# Revit family: VZ-PORTA-FERRO SIMPLES
name_source: partatom
category: Doors
units: mm (PartAtom-declared; Revit-internal decimal feet)

## family parameters
Always vertical = Yes
Cut with Voids When Loaded = No
Host = Wall
OmniClass Number = 23.30.10.00
OmniClass Title = Doors
Room Calculation Point = No
Shared = No

## types (2) — shared parameters
Altura_Fechadura = 110 cm
Altura_Folha = 213.5 cm
Analytic Construction = <Nenhum>
Batente = 4 cm
Esp_Folha = 3.7 cm
Esp_Marco = 3.5 cm
Esp_Perfil = 0.5 cm
Function = Interior
Height = 210 cm
Largura_Folha = 87 cm
Mat_Batente = .VZ-PINTURA-ESMALTE-BRANCO CORAL CORALIT
Mat_Fechadura = .VZ-METAL-AÇO INOXIDÁVEL
Mat_Folha = .VZ-PINTURA-ESMALTE-BRANCO CORAL CORALIT
PT_ALTURA OSSO = 214 cm
PT_FECHADURAS TETRA = Yes
PT_LARGURA OSSO = 88 cm
PT_MOLA_AEREA = Yes
PT_TIPO = FERRO
Profundidade_Perfil = 4 cm
Rough Height = 214 cm
Rough Width = 88 cm
VZA_ACESSIBILIDADE = No
Wall Closure = By host
Width = 80 cm

## per-type parameters (varying)
| type | Description | Deslocamento_Fechadura | PT_HDL_C90 | PT_MAÇANETA_DESIGN_420 | PT_PUXADOR_FIXO | VZA_CODIGO CLIENTE |
| PF01-80x210 | PORTA CEGA, 01 FOLHA DE ABRIR EM AÇO DUPLA LISA, REVESTIDA EM ESMALTE BRANCO CORAL CORALIT E FIXADA COM GRAPAS METÁLICAS, COM FECHO ELÉTRICO 12V EMBUTIDO NO MARCO HDL C90 E PUXADOR FIXO PAPAIZ  (REF. 500, ACABAMENTO ACETINADO) TANTO NO LADO EXTERNO QUANTO NO LADO INTERNO DA PORTA, COM MOLA AÉREA DORMA POTÊNCIA 2, DUAS FECHADURAS TETRA COM A MESMA COMBINAÇÃO | 4.35 cm | Yes | No | Yes | PF01 |
| PF02-80x210 | PORTA CEGA, 1 FOLHA DE ABRIR DE AÇO, REVESTIDA EM ESMALTE BRANCO CORAL CORALIT, DOBRADIÇA PAPAIZ  MODELO 1296 DE AÇO INOX 76X63MM ACETINADA, MAÇANETA E FECHADURA PAPAIZ (REF. DESIGN 420 ACETINADA) COM DUAS FECHADURAS TETRA COM A MESMA COMBINAÇÃO. MOLA AÉREA DORMA POTÊNCIA 2. | 8.2 cm | No | Yes | No | PF02 |

## geometry (parser evidence)
native form markers: Sweep x3
no freeform markers — native parametric forms only
